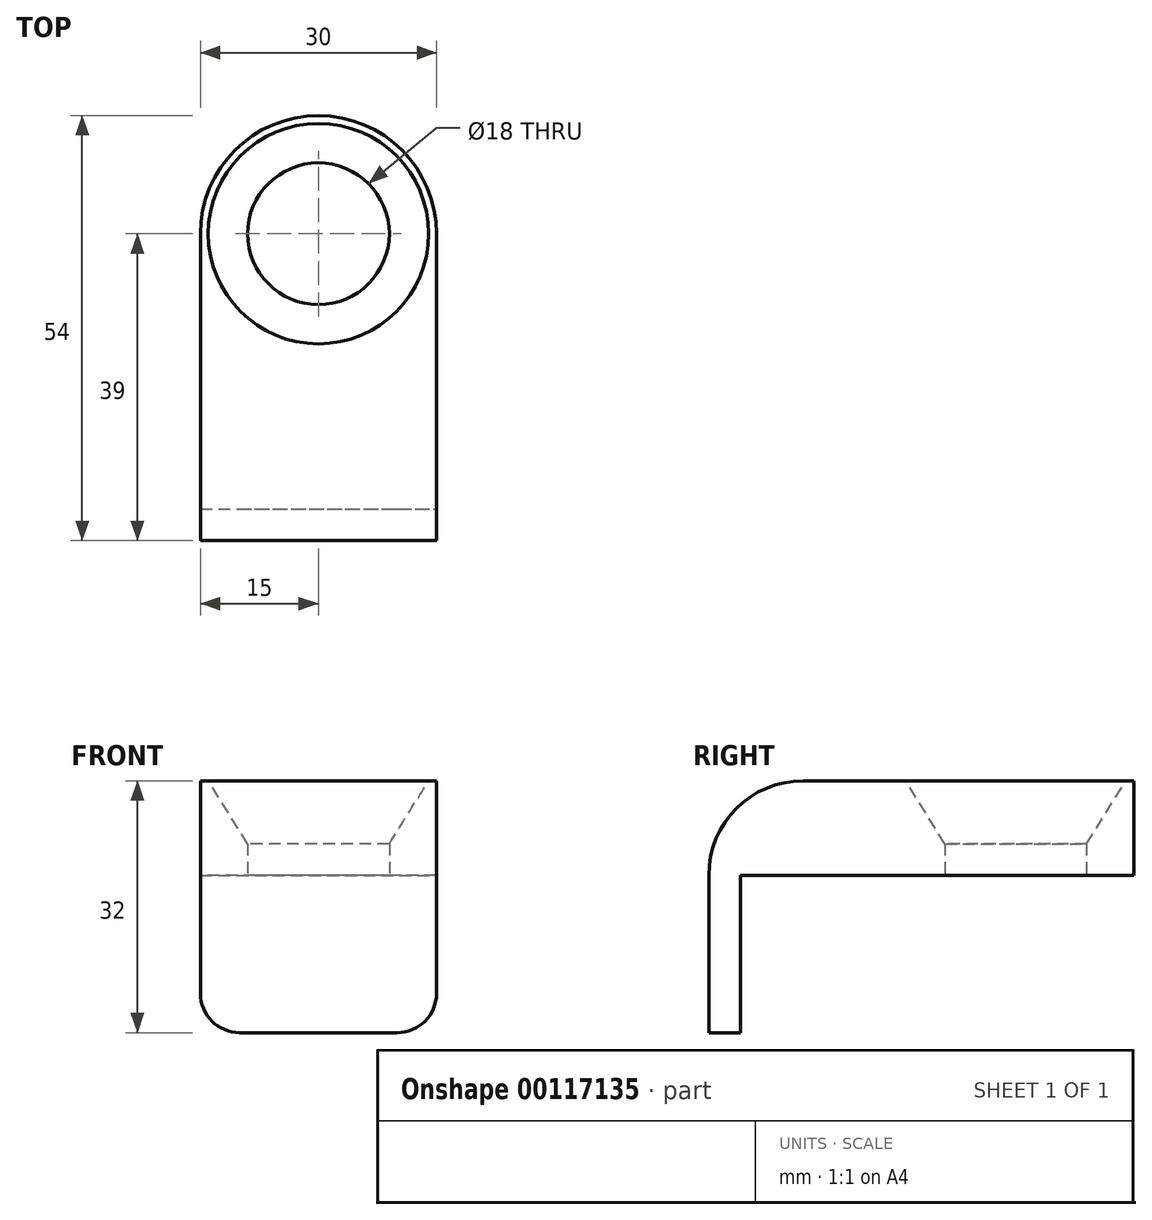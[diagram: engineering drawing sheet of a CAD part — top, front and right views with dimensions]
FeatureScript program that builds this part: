
annotation { "Feature Type Name" : "Feature", "Feature Type Description" : "" }
export const myFeature = defineFeature(function(context is Context, id is Id, definition is map)
    precondition{}
    {
        {
            var Q0;
            Q0=qCreatedBy(makeId("Top.planeOp"),FACE);
            var sketch = newSketch(context, id + "F0", { "sketchPlane" : qUnion([Q0])});
            skCircle(sketch, "E0", {"center": v(0, 0) * mm, "radius": 9 * mm});
            skArc(sketch, "E1", {"start": v(15, 0) * mm, "mid": v(0, 15) * mm, "end": v(-15, 0) * mm});
            skLineSegment(sketch, "E2", {"start": v(-15, 0) * mm, "end": v(-15, -39) * mm});
            skLineSegment(sketch, "E3", {"start": v(-15, -39) * mm, "end": v(15, -39) * mm});
            skLineSegment(sketch, "E4", {"start": v(15, -39) * mm, "end": v(15, 0) * mm});
            skLineSegment(sketch, "E5", {"start": v(-15, -35) * mm, "end": v(15, -35) * mm});
            skCircle(sketch, "E6", {"center": v(0, 0) * mm, "radius": 12 * mm});
            skSolve(sketch);
        }
        {
            var Q0;
            {var subQ2=sQuery(id+"F0.wireOp",EDGE,"E1");Q0=makeQuery(id+"F0.imprint","IMPRINT",FACE,{"disambiguationData":[TD([[makeQuery(id+"F0.imprint","IMPRINT",EDGE,{"derivedFrom":subQ2}),1.0]])]});}
            var Q1;
            {var subQ0=sQuery(id+"F0.wireOp",EDGE,"E3");Q1=makeQuery(id+"F0.imprint","IMPRINT",FACE,{"disambiguationData":[TD([[makeQuery(id+"F0.imprint","IMPRINT",EDGE,{"derivedFrom":subQ0}),1.0]])]});}
            var Q2;
            Q2=makeQuery(id+"F0.imprint","IMPRINT",FACE,{"disambiguationData":[TD([[makeQuery(id+"F0.imprint","IMPRINT",EDGE,{"derivedFrom":sQuery(id+"F0.wireOp",EDGE,"E0")}),-1.0]])]});
            extrude(context, id + "F1", {"entities" : qUnion([Q0, Q1, Q2]), "depth" : 3 * mm});
        }
        {
            var Q0;
            {var subQ0=sQuery(id+"F0.wireOp",EDGE,"E3");Q0=makeQuery(id+"F0.imprint","IMPRINT",FACE,{"disambiguationData":[TD([[makeQuery(id+"F0.imprint","IMPRINT",EDGE,{"derivedFrom":subQ0}),1.0]])]});}
            extrude(context, id + "F2", {"entities" : qUnion([Q0]), "operationType" : NewBodyOperationType.ADD, "oppositeDirection" : true, "depth" : 20 * mm});
        }
        {
            var Q0;
            Q0=makeQuery(id+"F0.imprint","IMPRINT",FACE,{"disambiguationData":[TD([[makeQuery(id+"F0.imprint","IMPRINT",EDGE,{"derivedFrom":sQuery(id+"F0.wireOp",EDGE,"E0")}),-1.0]])]});
            extrude(context, id + "F3", {"entities" : qUnion([Q0]), "operationType" : NewBodyOperationType.ADD, "depth" : 6 * mm});
        }
        {
            var Q0;
            Q0=makeQuery(id+"F3.boolean.opBoolean","INTERSECT",EDGE,{"derivedFrom":[makeQuery(id+"F1.opExtrude","CAP_FACE",FACE,{"disambiguationData":[OSD([sQuery(id+"F0.wireOp",EDGE,"E0"),sQuery(id+"F0.wireOp",EDGE,"E1"),sQuery(id+"F0.wireOp",EDGE,"E2"),sQuery(id+"F0.wireOp",EDGE,"E3"),sQuery(id+"F0.wireOp",EDGE,"E4")])],"isStart":false}),makeQuery(id+"F3.opExtrude","SWEPT_FACE",FACE,{"disambiguationData":[OSD([sQuery(id+"F0.wireOp",EDGE,"E6")])]})]});
            chamfer(context, id + "F4", {"entities" : qUnion([Q0]), "width" : 3 * mm, "tangentPropagation" : true});
        }
        {
            var Q0;
            {var subQ2=sQuery(id+"F0.wireOp",EDGE,"E1");Q0=makeQuery(id+"F0.imprint","IMPRINT",FACE,{"disambiguationData":[TD([[makeQuery(id+"F0.imprint","IMPRINT",EDGE,{"derivedFrom":subQ2}),1.0]])]});}
            var sketch = newSketch(context, id + "F5", { "sketchPlane" : qUnion([Q0])});
            skSolve(sketch);
        }
        {
            var Q0;
            Q0 = qSketchRegion(id + "F5", true);
            var Q1;
            {var subQ2=sQuery(id+"F0.wireOp",EDGE,"E1");Q1=makeQuery(id+"F0.imprint","IMPRINT",FACE,{"disambiguationData":[TD([[makeQuery(id+"F0.imprint","IMPRINT",EDGE,{"derivedFrom":subQ2}),1.0]])]});}
            var Q2;
            Q2=makeQuery(id+"F0.imprint","IMPRINT",FACE,{"disambiguationData":[TD([[makeQuery(id+"F0.imprint","IMPRINT",EDGE,{"derivedFrom":sQuery(id+"F0.wireOp",EDGE,"E0")}),-1.0]])]});
            extrude(context, id + "F6", {"entities" : qUnion([Q0, Q1, Q2]), "operationType" : NewBodyOperationType.ADD, "depth" : 12 * mm});
        }
        {
            var Q0;
            Q0=makeQuery(id+"F6.opExtrude","CAP_EDGE",EDGE,{"disambiguationData":[OSD([sQuery(id+"F0.wireOp",EDGE,"E0")])],"isStart":false});
            chamfer(context, id + "F7", {"entities" : qUnion([Q0]), "chamferType" : ChamferType.TWO_OFFSETS, "width1" : 8 * mm, "oppositeDirection" : false, "width2" : 5 * mm, "tangentPropagation" : true});
        }
        {
            var Q0;
            Q0=makeQuery(id+"F6.opExtrude","SWEPT_FACE",FACE,{"disambiguationData":[OSD([sQuery(id+"F0.wireOp",EDGE,"E5")])]});
            var Q1;
            {var subQ0=sQuery(id+"F0.wireOp",EDGE,"E3");Q1=makeQuery(id+"F2.boolean.opBoolean","MERGE",FACE,{"derivedFrom":[makeQuery(id+"F1.opExtrude","SWEPT_FACE",FACE,{"disambiguationData":[OSD([subQ0])]}),makeQuery(id+"F2.opExtrude","SWEPT_FACE",FACE,{"disambiguationData":[OSD([subQ0])]})]});}
            extrude(context, id + "F8", {"entities" : qUnion([Q0]), "operationType" : NewBodyOperationType.ADD, "endBound" : BoundingType.UP_TO_SURFACE, "endBoundEntityFace" : qUnion([Q1]), "depth" : 25 * mm});
        }
        {
            var Q0;
            Q0=makeQuery(id+"F8.opExtrude","CAP_EDGE",EDGE,{"disambiguationData":[OSD([sQuery(id+"F0.wireOp",EDGE,"E5")])],"isStart":false});
            fillet(context, id + "F9", {"entities" : qUnion([Q0]), "radius" : 12 * mm, "tangentPropagation" : true, "allowEdgeOverflow" : false});
        }
        {
            var Q0;
            Q0=makeQuery(id+"F2.opExtrude","CAP_EDGE",EDGE,{"disambiguationData":[OSD([sQuery(id+"F0.wireOp",EDGE,"E2")])],"isStart":false});
            var Q1;
            Q1=makeQuery(id+"F2.opExtrude","CAP_EDGE",EDGE,{"disambiguationData":[OSD([sQuery(id+"F0.wireOp",EDGE,"E4")])],"isStart":false});
            fillet(context, id + "F10", {"entities" : qUnion([Q0, Q1]), "radius" : 5 * mm, "tangentPropagation" : true, "allowEdgeOverflow" : false});
        }
    });
